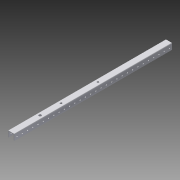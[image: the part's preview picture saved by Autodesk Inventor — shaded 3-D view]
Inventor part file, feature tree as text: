
AUTODESK INVENTOR PART (.ipt)
format: ipt  version: 2015 (Build 190159000, 159)  size: 282,112 bytes
history: native  units: in
note: dims shown in document units (in); Inventor stores cm internally (conversion verified against a paired STEP export)
features: extrude x3, sketch x3, pattern_linear x1, projected_geometry x1
ambient origin geometry x8: Origin, YZ Plane, XZ Plane, XY Plane, X Axis, Y Axis, Z Axis, Center Point
bodies: Solid1 (feature_tree)
feature tree (8):
  extrude  "Extrusion1"  Depth=30.0in
  extrude  "Extrusion4"  Depth=0.5in
  pattern_linear  "Rectangular Pattern3"  Spacing1=0.25in  [1 undecoded]
  extrude  "Extrusion5"  Depth=1.0in TaperAngle=0.0deg
  sketch  "Sketch1"  dims[d0=1.13in d1=1.25in d2=0.125in d3=0.125in d4=0.125in d5=30.0in]
  sketch  "Sketch4"  dims[d6=0.0in d35=0.5in]
  sketch  "Sketch5"  dims[d36=0.5in d37=0.25in d38=1.0in d39=0.0in d40=7.874in d42=1.0in d43=7.874in d45=1.0in d46=9.5in d47=0.375in d48=0.5in d49=0.375in d50=7.0in d51=0.5in d52=1.0in d53=0.0in d54=0.5in d55=5.5in d56=0.5in]
  projected_geometry  "Projected Loop1"
note: 1 required parameter value undecoded (feature->parameter linkage not recoverable at this tier; creation-order binding heuristic only, values carry confidence <= 0.55)
